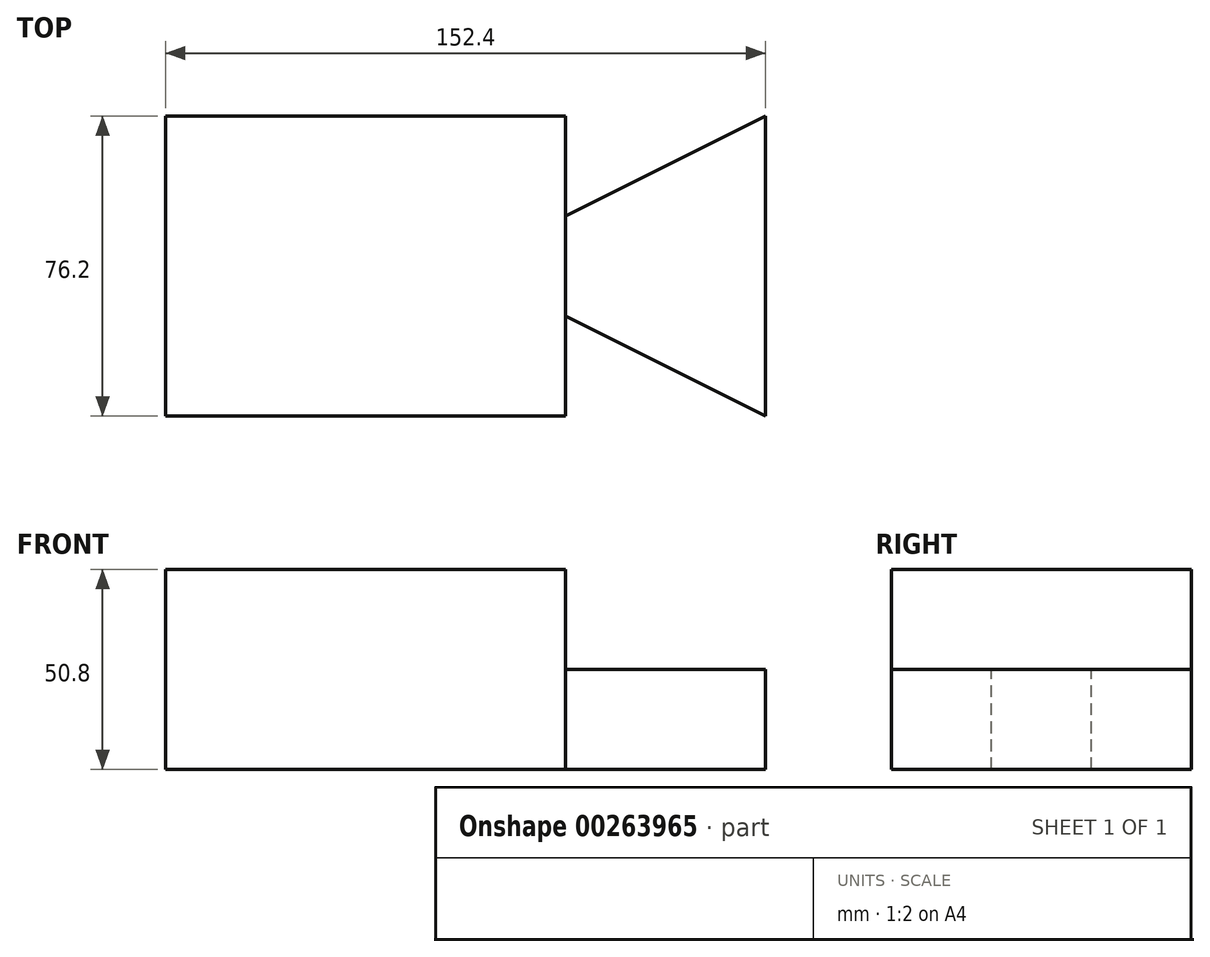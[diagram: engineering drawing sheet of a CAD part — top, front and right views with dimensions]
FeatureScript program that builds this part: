
annotation { "Feature Type Name" : "Feature", "Feature Type Description" : "" }
export const myFeature = defineFeature(function(context is Context, id is Id, definition is map)
    precondition{}
    {
        {
            var Q0;
            Q0=qCreatedBy(makeId("Front.planeOp"),FACE);
            var sketch = newSketch(context, id + "F0", { "sketchPlane" : qUnion([Q0])});
            skLineSegment(sketch, "E0", {"start": v(0, 0) * mm, "end": v(-101.6, 0) * mm});
            skLineSegment(sketch, "E1", {"start": v(-101.6, 0) * mm, "end": v(-101.6, 50.8) * mm});
            skLineSegment(sketch, "E2", {"start": v(-101.6, 50.8) * mm, "end": v(0, 50.8) * mm});
            skLineSegment(sketch, "E3", {"start": v(0, 50.8) * mm, "end": v(0, 0) * mm});
            skSolve(sketch);
        }
        {
            var Q0;
            Q0=makeQuery(id+"F0.imprint","IMPRINT",FACE,{"disambiguationData":[TD([[makeQuery(id+"F0.imprint","IMPRINT",EDGE,{"derivedFrom":sQuery(id+"F0.wireOp",EDGE,"E0")}),-1.0]])]});
            extrude(context, id + "F1", {"entities" : qUnion([Q0]), "oppositeDirection" : true, "depth" : 76.2 * mm});
        }
        {
            var Q0;
            Q0=qCreatedBy(makeId("Top.planeOp"),FACE);
            var sketch = newSketch(context, id + "F2", { "sketchPlane" : qUnion([Q0])});
            skLineSegment(sketch, "E4", {"start": v(0, 0) * mm, "end": v(50.8, 0) * mm});
            skLineSegment(sketch, "E5", {"start": v(50.8, 0) * mm, "end": v(50.8, 76.2) * mm});
            skLineSegment(sketch, "E6", {"start": v(50.8, 76.2) * mm, "end": v(0, 76.2) * mm});
            skLineSegment(sketch, "E7", {"start": v(0, 76.2) * mm, "end": v(0, 0) * mm});
            skSolve(sketch);
        }
        {
            var Q0;
            Q0=makeQuery(id+"F2.imprint","IMPRINT",FACE,{"disambiguationData":[TD([[makeQuery(id+"F2.imprint","IMPRINT",EDGE,{"derivedFrom":sQuery(id+"F2.wireOp",EDGE,"E4")}),1.0]])]});
            extrude(context, id + "F3", {"entities" : qUnion([Q0]), "operationType" : NewBodyOperationType.ADD, "depth" : 25.4 * mm});
        }
        {
            var Q0;
            Q0=makeQuery(id+"F3.opExtrude","CAP_FACE",FACE,{"disambiguationData":[OSD([sQuery(id+"F2.wireOp",EDGE,"E4"),sQuery(id+"F2.wireOp",EDGE,"E5"),sQuery(id+"F2.wireOp",EDGE,"E6"),sQuery(id+"F2.wireOp",EDGE,"E7")])],"isStart":false});
            var sketch = newSketch(context, id + "F4", { "sketchPlane" : qUnion([Q0])});
            skLineSegment(sketch, "E8", {"start": v(0, 0) * mm, "end": v(50.8, 0) * mm});
            skLineSegment(sketch, "E9", {"start": v(0, 0) * mm, "end": v(0, 25.4) * mm});
            skLineSegment(sketch, "E10", {"start": v(0, 25.4) * mm, "end": v(50.8, 0) * mm});
            skLineSegment(sketch, "E11", {"start": v(50.8, 38.1) * mm, "end": v(0, 38.1) * mm, "construction": true});
            skLineSegment(sketch, "E12.MirrorCS", {"start": v(0, 50.8) * mm, "end": v(50.8, 76.2) * mm});
            skLineSegment(sketch, "E13.MirrorCS", {"start": v(0, 76.2) * mm, "end": v(0, 50.8) * mm});
            skLineSegment(sketch, "E14.MirrorCS", {"start": v(0, 76.2) * mm, "end": v(50.8, 76.2) * mm});
            skSolve(sketch);
        }
        {
            var Q0;
            Q0=makeQuery(id+"F4.imprint","IMPRINT",FACE,{"disambiguationData":[TD([[makeQuery(id+"F4.imprint","IMPRINT",EDGE,{"derivedFrom":sQuery(id+"F4.wireOp",EDGE,"E8")}),1.0]])]});
            var Q1;
            Q1=makeQuery(id+"F4.imprint","IMPRINT",FACE,{"disambiguationData":[TD([[makeQuery(id+"F4.imprint","IMPRINT",EDGE,{"derivedFrom":sQuery(id+"F4.wireOp",EDGE,"E12.MirrorCS")}),1.0]])]});
            extrude(context, id + "F5", {"entities" : qUnion([Q0, Q1]), "operationType" : NewBodyOperationType.REMOVE, "endBound" : BoundingType.UP_TO_NEXT, "oppositeDirection" : true, "depth" : 25.4 * mm});
        }
    });
